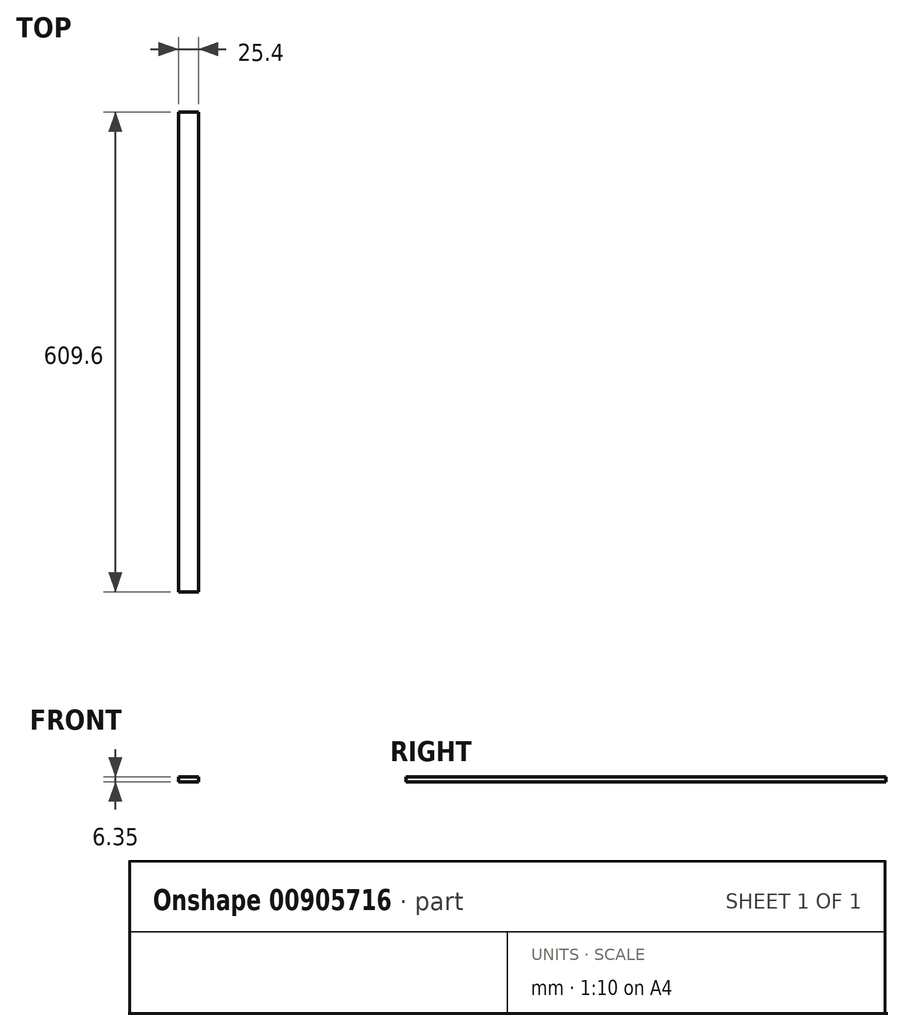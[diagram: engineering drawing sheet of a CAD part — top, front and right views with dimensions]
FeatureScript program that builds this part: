
annotation { "Feature Type Name" : "Feature", "Feature Type Description" : "" }
export const myFeature = defineFeature(function(context is Context, id is Id, definition is map)
    precondition{}
    {
        {
            var Q0;
            Q0=qCreatedBy(makeId("Right.planeOp"),FACE);
            var sketch = newSketch(context, id + "F0", { "sketchPlane" : qUnion([Q0])});
            skLineSegment(sketch, "E0.bottom", {"start": v(-45.64, 20) * mm, "end": v(563.96, 20) * mm});
            skLineSegment(sketch, "E0.top", {"start": v(-45.64, 13.65) * mm, "end": v(563.96, 13.65) * mm});
            skLineSegment(sketch, "E0.left", {"start": v(-45.64, 20) * mm, "end": v(-45.64, 13.65) * mm});
            skLineSegment(sketch, "E0.right", {"start": v(563.96, 20) * mm, "end": v(563.96, 13.65) * mm});
            skSolve(sketch);
        }
        {
            var Q0;
            Q0 = qSketchRegion(id + "F0", true);
            extrude(context, id + "F1", {"entities" : qUnion([Q0]), "depth" : 25.4 * mm, "offsetDistance" : 25.4 * mm});
        }
    });
